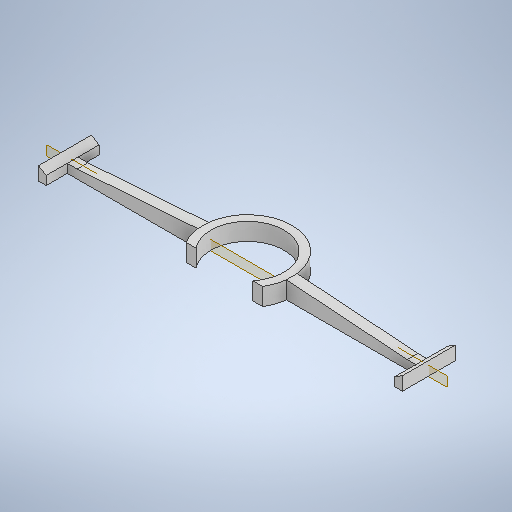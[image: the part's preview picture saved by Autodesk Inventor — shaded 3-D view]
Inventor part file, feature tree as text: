
AUTODESK INVENTOR PART (.ipt)
format: ipt  version: 2025.1 (Build 291241000, 241)  size: 340,480 bytes
history: native  units: mm
features: extrude x6, sketch x6, plane x1
ambient origin geometry x8: Origin, YZ Plane, XZ Plane, XY Plane, X Axis, Y Axis, Z Axis, Center Point
bodies: Volumenkörper1 (feature_tree)
feature tree (13):
  extrude  "Extrusion1"  Depth=2.85mm
  plane  "Arbeitsebene1"
  extrude  "Extrusion2"  Depth=2.85mm
  extrude  "Extrusion3"  Depth=19.7mm
  extrude  "Extrusion4"  Depth=6.5mm TaperAngle=0.0deg
  extrude  "Extrusion7"  Depth=45.0mm
  extrude  "Extrusion8"  Depth=3.25mm TaperAngle=0.0deg
  sketch  "Skizze1"  dims[d0=135.6mm d1=4.0mm d2=3.25mm d3=0.0mm d4=2.85mm]
  sketch  "Skizze2"  dims[d5=1.75mm d6=2.85mm]
  sketch  "Skizze3"  dims[d7=19.7mm d8=0.0mm d9=32.0mm]
  sketch  "Skizze4"  dims[d10=0.0mm d11=0.0mm d15=6.5mm d16=0.0mm]
  sketch  "Skizze7"  dims[d27=3.0mm d28=27.25mm d29=8.6mm d30=45.0mm]
  sketch  "Skizze8"  dims[d31=45.0mm d32=3.25mm d33=0.0mm d34=0.0mm d35=0.0mm d17=0.5mm d18=0.872665mm]
